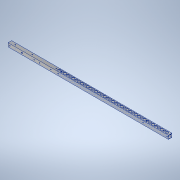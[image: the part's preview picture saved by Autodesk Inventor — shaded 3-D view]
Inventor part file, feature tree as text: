
AUTODESK INVENTOR PART (.ipt)
format: ipt  version: 2020.3 (Build 243373000, 373)  size: 282,112 bytes
history: native  units: mm
features: sketch x11, hole x8, extrude x3, other x1
ambient origin geometry x8: Origin, YZ Plane, XZ Plane, XY Plane, X Axis, Y Axis, Z Axis, Center Point
bodies: Body1 (feature_tree)
feature tree (23):
  other  "ソリッド1"
  extrude  "押し出し1"  Depth=15.0mm
  hole  "穴1"  [1 undecoded]
  hole  "穴2"  [1 undecoded]
  hole  "穴3"  [1 undecoded]
  extrude  "押し出し2"  Depth=1.2mm
  hole  "穴4"  [1 undecoded]
  hole  "穴5"  [1 undecoded]
  hole  "穴6"  [1 undecoded]
  extrude  "押し出し3"  Depth=7.5mm
  hole  "穴8"  [1 undecoded]
  hole  "穴9"  [1 undecoded]
  sketch  "スケッチ1"
  sketch  "スケッチ2"
  sketch  "スケッチ3"
  sketch  "スケッチ4"
  sketch  "スケッチ5"
  sketch  "スケッチ6"
  sketch  "スケッチ7"
  sketch  "スケッチ8"
  sketch  "スケッチ11"
  sketch  "スケッチ12"
  sketch  "スケッチ13"
note: 8 required parameter values undecoded (feature->parameter linkage not recoverable at this tier; creation-order binding heuristic only, values carry confidence <= 0.55)
